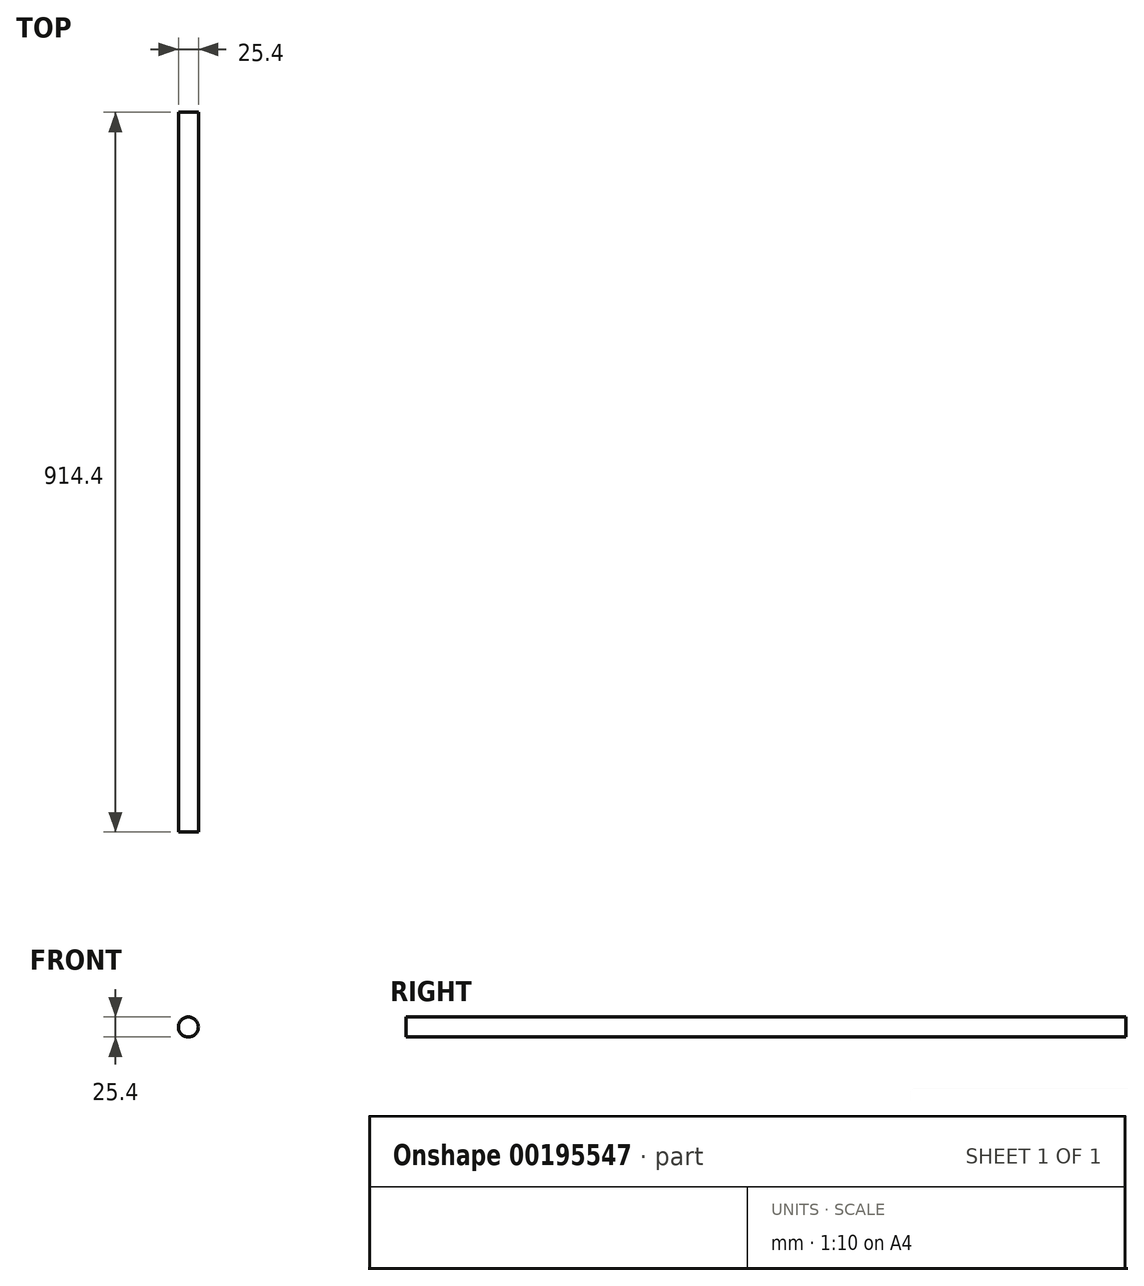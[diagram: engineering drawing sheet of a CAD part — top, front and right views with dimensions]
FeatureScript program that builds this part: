
annotation { "Feature Type Name" : "Feature", "Feature Type Description" : "" }
export const myFeature = defineFeature(function(context is Context, id is Id, definition is map)
    precondition{}
    {
        {
            var Q0;
            Q0=qCreatedBy(makeId("Front.planeOp"),FACE);
            var sketch = newSketch(context, id + "F0", { "sketchPlane" : qUnion([Q0])});
            skCircle(sketch, "E0", {"center": v(0, 0) * mm, "radius": 12.7 * mm});
            skSolve(sketch);
        }
        {
            var Q0;
            Q0 = qSketchRegion(id + "F0", true);
            extrude(context, id + "F1", {"entities" : qUnion([Q0]), "oppositeDirection" : true, "depth" : 914.4 * mm});
        }
    });
